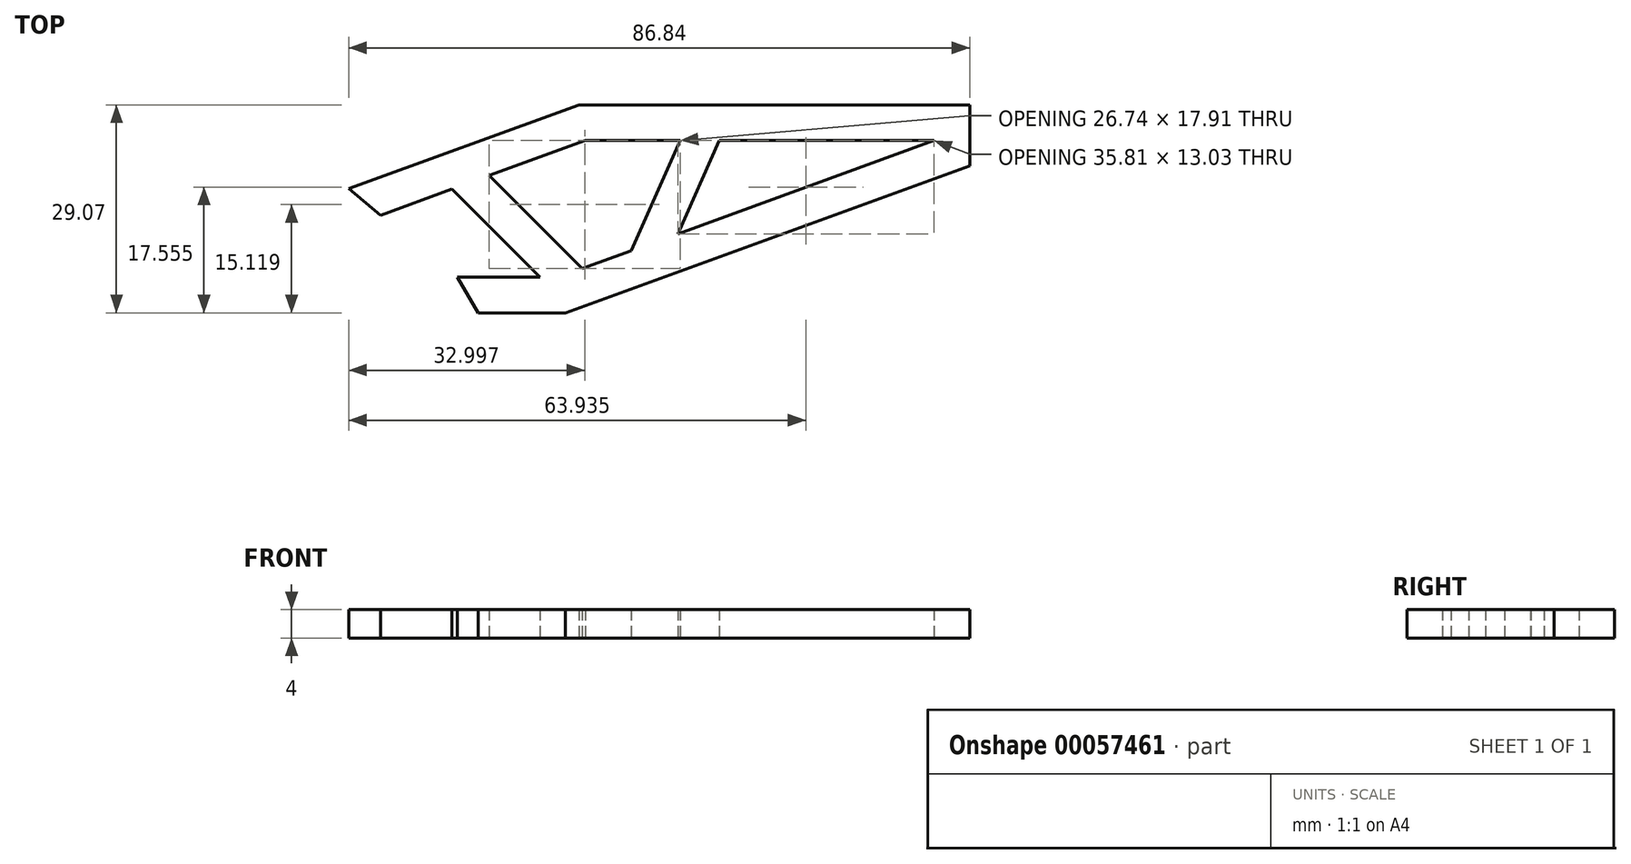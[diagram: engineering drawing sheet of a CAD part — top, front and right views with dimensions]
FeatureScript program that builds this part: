
annotation { "Feature Type Name" : "Feature", "Feature Type Description" : "" }
export const myFeature = defineFeature(function(context is Context, id is Id, definition is map)
    precondition{}
    {
        {
            var Q0;
            Q0=qCreatedBy(makeId("Top.planeOp"),FACE);
            var sketch = newSketch(context, id + "F0", { "sketchPlane" : qUnion([Q0])});
            skLineSegment(sketch, "E0.bottom", {"start": v(-13, 6.75) * mm, "end": v(13, 6.75) * mm, "construction": true});
            skLineSegment(sketch, "E0.top", {"start": v(-14, 0) * mm, "end": v(14, 0) * mm, "construction": true});
            skLineSegment(sketch, "E0.left", {"start": v(-13, 6.75) * mm, "end": v(-14, 0) * mm, "construction": true});
            skLineSegment(sketch, "E0.right", {"start": v(13, 6.75) * mm, "end": v(14, 0) * mm, "construction": true});
            skPoint(sketch, "E1", {"position": v(0, 6.75) * mm});
            skPoint(sketch, "E2", {"position": v(0, 0) * mm});
            skLineSegment(sketch, "E3", {"start": v(-12.46, 0) * mm, "end": v(-13.87, -4) * mm, "construction": true});
            skLineSegment(sketch, "E4", {"start": v(-13.88, -4) * mm, "end": v(13.88, -4) * mm, "construction": true});
            skLineSegment(sketch, "E5", {"start": v(13.87, -4) * mm, "end": v(12.47, 0) * mm, "construction": true});
            skLineSegment(sketch, "E6", {"start": v(-12.46, 0) * mm, "end": v(12.46, 0) * mm, "construction": true});
            skPoint(sketch, "E7", {"position": v(0, -4) * mm});
            skLineSegment(sketch, "E8", {"start": v(13, -0.56) * mm, "end": v(24.54, -0.56) * mm});
            skLineSegment(sketch, "E9", {"start": v(13, -0.56) * mm, "end": v(15.88, -5.56) * mm});
            skLineSegment(sketch, "E10", {"start": v(24.54, -0.56) * mm, "end": v(16.54, 13.3) * mm, "construction": true});
            skLineSegment(sketch, "E11", {"start": v(16.54, 13.3) * mm, "end": v(2.22, 8.09) * mm, "construction": true});
            skLineSegment(sketch, "E12", {"start": v(-2.2, 11.8) * mm, "end": v(29.99, 23.51) * mm});
            skLineSegment(sketch, "E13", {"start": v(29.99, 23.51) * mm, "end": v(84.64, 23.51) * mm});
            skLineSegment(sketch, "E14", {"start": v(84.64, 23.51) * mm, "end": v(84.64, 15.01) * mm});
            skLineSegment(sketch, "E15", {"start": v(84.64, 15.01) * mm, "end": v(28.12, -5.56) * mm});
            skLineSegment(sketch, "E16", {"start": v(28.12, -5.56) * mm, "end": v(15.88, -5.56) * mm});
            skLineSegment(sketch, "E17", {"start": v(49.64, 18.51) * mm, "end": v(79.64, 18.51) * mm});
            skLineSegment(sketch, "E18", {"start": v(79.64, 18.51) * mm, "end": v(43.83, 5.48) * mm});
            skLineSegment(sketch, "E19", {"start": v(43.83, 5.48) * mm, "end": v(49.64, 18.51) * mm});
            skLineSegment(sketch, "E20", {"start": v(44.17, 18.51) * mm, "end": v(37.3, 3.1) * mm});
            skLineSegment(sketch, "E21", {"start": v(37.3, 3.1) * mm, "end": v(30.44, 0.6) * mm});
            skLineSegment(sketch, "E22", {"start": v(29.78, 0.36) * mm, "end": v(21.3, 15.03) * mm, "construction": true});
            skLineSegment(sketch, "E23", {"start": v(21.3, 15.03) * mm, "end": v(30.87, 18.51) * mm});
            skLineSegment(sketch, "E24", {"start": v(30.87, 18.51) * mm, "end": v(44.17, 18.51) * mm});
            skLineSegment(sketch, "E25", {"start": v(46.95, 6.62) * mm, "end": v(48.66, 1.92) * mm, "construction": true});
            skLineSegment(sketch, "E26", {"start": v(16.98, 12.53) * mm, "end": v(21.3, 15.03) * mm, "construction": true});
            skLineSegment(sketch, "E27", {"start": v(64.64, 18.51) * mm, "end": v(64.64, 23.51) * mm, "construction": true});
            skLineSegment(sketch, "E28", {"start": v(79.64, 18.51) * mm, "end": v(81.35, 13.81) * mm, "construction": true});
            skLineSegment(sketch, "E29", {"start": v(44.17, 18.51) * mm, "end": v(48.73, 16.48) * mm, "construction": true});
            skLineSegment(sketch, "E30", {"start": v(15.88, -0.56) * mm, "end": v(15.88, -5.56) * mm, "construction": true});
            skLineSegment(sketch, "E31", {"start": v(24.54, -0.56) * mm, "end": v(28.12, -5.56) * mm, "construction": true});
            skLineSegment(sketch, "E32", {"start": v(29.78, 0.36) * mm, "end": v(28.12, -5.56) * mm, "construction": true});
            skLineSegment(sketch, "E33", {"start": v(16.54, 13.3) * mm, "end": v(21.3, 15.03) * mm, "construction": true});
            skLineSegment(sketch, "E34", {"start": v(30.87, 18.51) * mm, "end": v(30.87, 23.51) * mm, "construction": true});
            skLineSegment(sketch, "E35", {"start": v(28.14, 17.52) * mm, "end": v(26.43, 22.22) * mm, "construction": true});
            skLineSegment(sketch, "E36", {"start": v(2.22, 8.09) * mm, "end": v(0.51, 12.79) * mm, "construction": true});
            skLineSegment(sketch, "E37", {"start": v(-2.2, 11.8) * mm, "end": v(2.22, 8.09) * mm});
            skLineSegment(sketch, "E38", {"start": v(79.64, 18.51) * mm, "end": v(84.64, 18.51) * mm, "construction": true});
            skLineSegment(sketch, "E39", {"start": v(81.8, 20.67) * mm, "end": v(81.8, 17) * mm, "construction": true});
            skLineSegment(sketch, "E40", {"start": v(81.8, 17) * mm, "end": v(74.88, 14.49) * mm, "construction": true});
            skLineSegment(sketch, "E41", {"start": v(74.88, 14.49) * mm, "end": v(73.8, 20.67) * mm, "construction": true});
            skLineSegment(sketch, "E42", {"start": v(73.8, 20.67) * mm, "end": v(81.8, 20.67) * mm, "construction": true});
            skLineSegment(sketch, "E43", {"start": v(81.8, 20.67) * mm, "end": v(84.64, 20.67) * mm, "construction": true});
            skLineSegment(sketch, "E44", {"start": v(81.8, 20.67) * mm, "end": v(81.8, 23.51) * mm, "construction": true});
            skLineSegment(sketch, "E45", {"start": v(81.8, 17) * mm, "end": v(82.77, 14.33) * mm, "construction": true});
            skLineSegment(sketch, "E46", {"start": v(73.8, 20.67) * mm, "end": v(73.8, 23.51) * mm, "construction": true});
            skLineSegment(sketch, "E47", {"start": v(74.88, 14.49) * mm, "end": v(75.86, 11.81) * mm, "construction": true});
            skLineSegment(sketch, "E48", {"start": v(24.54, -0.56) * mm, "end": v(12.24, 11.73) * mm});
            skLineSegment(sketch, "E49", {"start": v(13.9, 10.08) * mm, "end": v(17.43, 13.62) * mm, "construction": true});
            skLineSegment(sketch, "E50", {"start": v(30.44, 0.6) * mm, "end": v(17.43, 13.62) * mm});
            skLineSegment(sketch, "E51", {"start": v(29.78, 0.36) * mm, "end": v(30.44, 0.6) * mm, "construction": true});
            skLineSegment(sketch, "E52", {"start": v(21.3, 15.03) * mm, "end": v(17.43, 13.62) * mm});
            skLineSegment(sketch, "E53", {"start": v(12.24, 11.73) * mm, "end": v(2.22, 8.09) * mm});
            skSolve(sketch);
        }
        {
            var Q0;
            Q0 = qSketchRegion(id + "F0", true);
            extrude(context, id + "F1", {"entities" : qUnion([Q0]), "depth" : 4 * mm});
        }
    });
